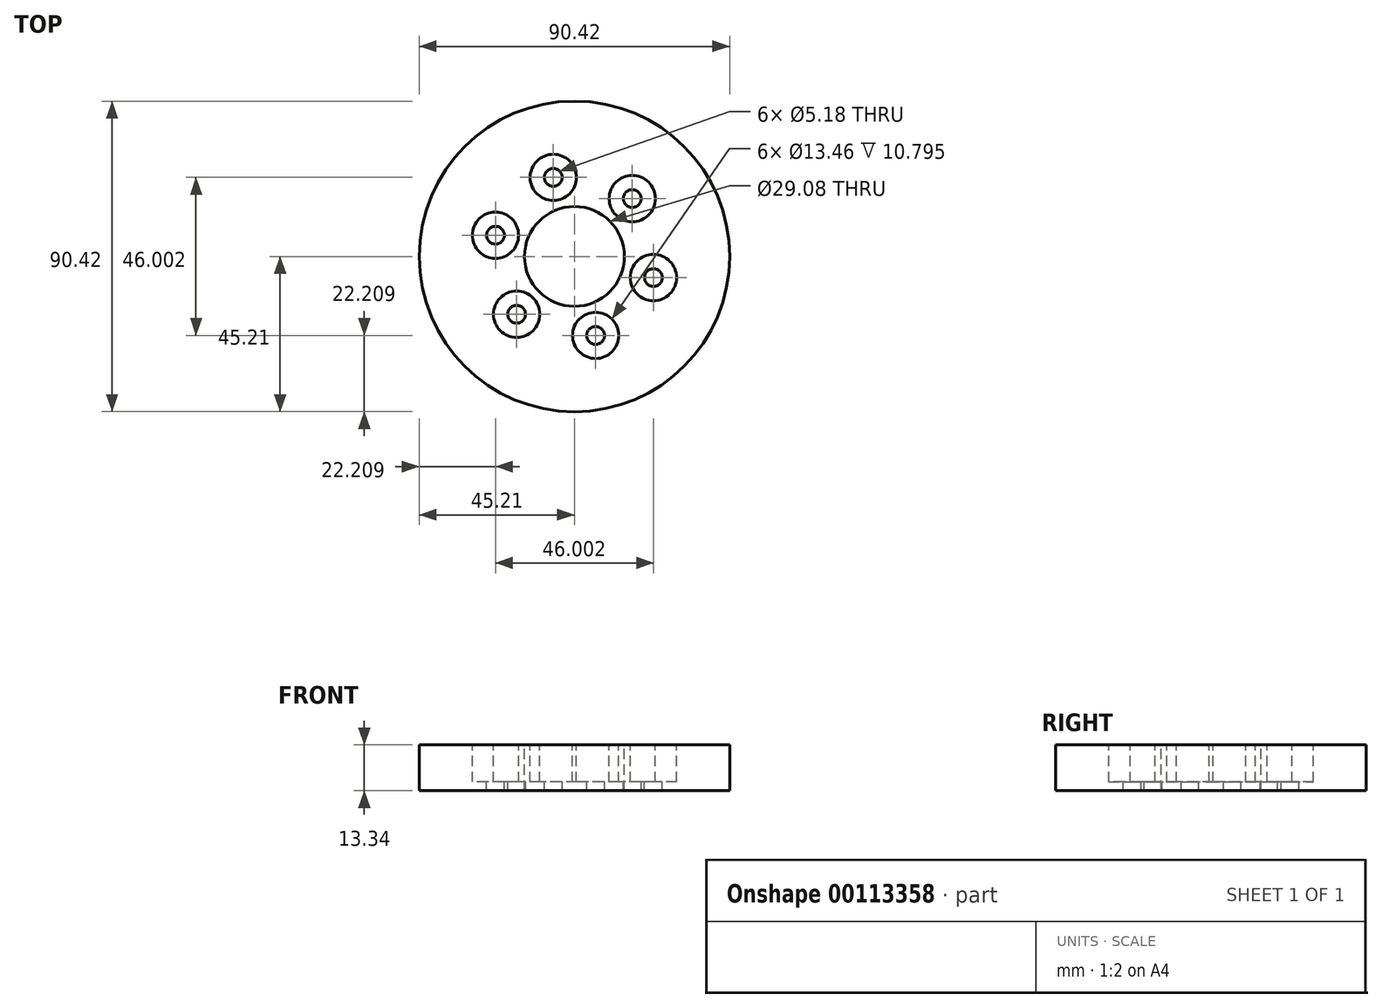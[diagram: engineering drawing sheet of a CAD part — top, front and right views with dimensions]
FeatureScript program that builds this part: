
annotation { "Feature Type Name" : "Feature", "Feature Type Description" : "" }
export const myFeature = defineFeature(function(context is Context, id is Id, definition is map)
    precondition{}
    {
        {
            var Q0;
            Q0=qCreatedBy(makeId("Top.planeOp"),FACE);
            var sketch = newSketch(context, id + "F0", { "sketchPlane" : qUnion([Q0])});
            skCircle(sketch, "E0", {"center": v(0, 0) * mm, "radius": 45.21 * mm});
            skSolve(sketch);
        }
        {
            var Q0;
            Q0=qSketchRegion(id+"F0",true);
            extrude(context, id + "F1", {"entities" : qUnion([Q0]), "depth" : 13.33 * mm, "offsetDistance" : 25.4 * mm});
        }
        {
            var Q0;
            Q0=makeQuery(id+"F1.opExtrude","CAP_FACE",FACE,{"disambiguationData":[OSD([sQuery(id+"F0.wireOp",EDGE,"E0")])],"isStart":false});
            var sketch = newSketch(context, id + "F2", { "sketchPlane" : qUnion([Q0])});
            skLineSegment(sketch, "E1", {"start": v(0, 0) * mm, "end": v(0, 60.06) * mm, "construction": true});
            skLineSegment(sketch, "E2", {"start": v(0, 0) * mm, "end": v(-13.99, 52.2) * mm, "construction": true});
            skCircle(sketch, "E3", {"center": v(0, 0) * mm, "radius": 23.81 * mm, "construction": true});
            skCircle(sketch, "E4", {"center": v(-6.16, 23) * mm, "radius": 2.6 * mm});
            skCircle(sketch, "E5.1.0", {"center": v(-23, 6.16) * mm, "radius": 2.6 * mm});
            skCircle(sketch, "E5.2.0", {"center": v(-16.84, -16.84) * mm, "radius": 2.6 * mm});
            skCircle(sketch, "E6.1.3.0", {"center": v(6.16, -23) * mm, "radius": 2.6 * mm});
            skCircle(sketch, "E6.1.4.0", {"center": v(23, -6.16) * mm, "radius": 2.6 * mm});
            skCircle(sketch, "E6.1.5.0", {"center": v(16.84, 16.84) * mm, "radius": 2.6 * mm});
            skLineSegment(sketch, "E7", {"start": v(0, 0) * mm, "end": v(16.84, 16.84) * mm, "construction": true});
            skSolve(sketch);
        }
        {
            var Q0;
            Q0=makeQuery(id+"F2.imprint","IMPRINT",FACE,{"disambiguationData":[TD([[makeQuery(id+"F2.imprint","IMPRINT",EDGE,{"derivedFrom":sQuery(id+"F2.wireOp",EDGE,"E4")}),1.0]])]});
            var Q1;
            Q1=makeQuery(id+"F2.imprint","IMPRINT",FACE,{"disambiguationData":[TD([[makeQuery(id+"F2.imprint","IMPRINT",EDGE,{"derivedFrom":sQuery(id+"F2.wireOp",EDGE,"E5.1.0")}),1.0]])]});
            var Q2;
            Q2=makeQuery(id+"F2.imprint","IMPRINT",FACE,{"disambiguationData":[TD([[makeQuery(id+"F2.imprint","IMPRINT",EDGE,{"derivedFrom":sQuery(id+"F2.wireOp",EDGE,"E5.2.0")}),1.0]])]});
            var Q3;
            Q3=makeQuery(id+"F2.imprint","IMPRINT",FACE,{"disambiguationData":[TD([[makeQuery(id+"F2.imprint","IMPRINT",EDGE,{"derivedFrom":sQuery(id+"F2.wireOp",EDGE,"E6.1.3.0")}),1.0]])]});
            var Q4;
            Q4=makeQuery(id+"F2.imprint","IMPRINT",FACE,{"disambiguationData":[TD([[makeQuery(id+"F2.imprint","IMPRINT",EDGE,{"derivedFrom":sQuery(id+"F2.wireOp",EDGE,"E6.1.4.0")}),1.0]])]});
            var Q5;
            Q5=makeQuery(id+"F2.imprint","IMPRINT",FACE,{"disambiguationData":[TD([[makeQuery(id+"F2.imprint","IMPRINT",EDGE,{"derivedFrom":sQuery(id+"F2.wireOp",EDGE,"E6.1.5.0")}),1.0]])]});
            extrude(context, id + "F3", {"entities" : qUnion([Q0, Q1, Q2, Q3, Q4, Q5]), "operationType" : NewBodyOperationType.REMOVE, "oppositeDirection" : true, "depth" : 25.4 * mm});
        }
        {
            var Q0;
            Q0=makeQuery(id+"F2.imprint","IMPRINT",FACE,{"disambiguationData":[TD([[makeQuery(id+"F2.imprint","IMPRINT",EDGE,{"derivedFrom":sQuery(id+"F2.wireOp",EDGE,"E4")}),-1.0]])]});
            var sketch = newSketch(context, id + "F4", { "sketchPlane" : qUnion([Q0])});
            skCircle(sketch, "E8", {"center": v(0, 0) * mm, "radius": 14.54 * mm});
            skSolve(sketch);
        }
        {
            var Q0;
            Q0=qSketchRegion(id+"F4",true);
            extrude(context, id + "F5", {"entities" : qUnion([Q0]), "operationType" : NewBodyOperationType.REMOVE, "oppositeDirection" : true, "depth" : 25.4 * mm});
        }
        {
            var Q0;
            Q0=makeQuery(id+"F2.imprint","IMPRINT",FACE,{"disambiguationData":[TD([[makeQuery(id+"F2.imprint","IMPRINT",EDGE,{"derivedFrom":sQuery(id+"F2.wireOp",EDGE,"E4")}),-1.0]])]});
            var sketch = newSketch(context, id + "F6", { "sketchPlane" : qUnion([Q0])});
            skCircle(sketch, "E9", {"center": v(-6.16, 23) * mm, "radius": 6.73 * mm});
            skCircle(sketch, "E10", {"center": v(16.84, 16.84) * mm, "radius": 6.73 * mm});
            skCircle(sketch, "E11", {"center": v(23, -6.16) * mm, "radius": 6.73 * mm});
            skCircle(sketch, "E12", {"center": v(6.16, -23) * mm, "radius": 6.73 * mm});
            skCircle(sketch, "E13", {"center": v(-16.84, -16.84) * mm, "radius": 6.73 * mm});
            skCircle(sketch, "E14", {"center": v(-23, 6.16) * mm, "radius": 6.73 * mm});
            skSolve(sketch);
        }
        {
            var Q0;
            Q0 = qSketchRegion(id + "F6", true);
            extrude(context, id + "F7", {"entities" : qUnion([Q0]), "operationType" : NewBodyOperationType.REMOVE, "oppositeDirection" : true, "depth" : 10.8 * mm, "offsetDistance" : 25.4 * mm});
        }
    });
